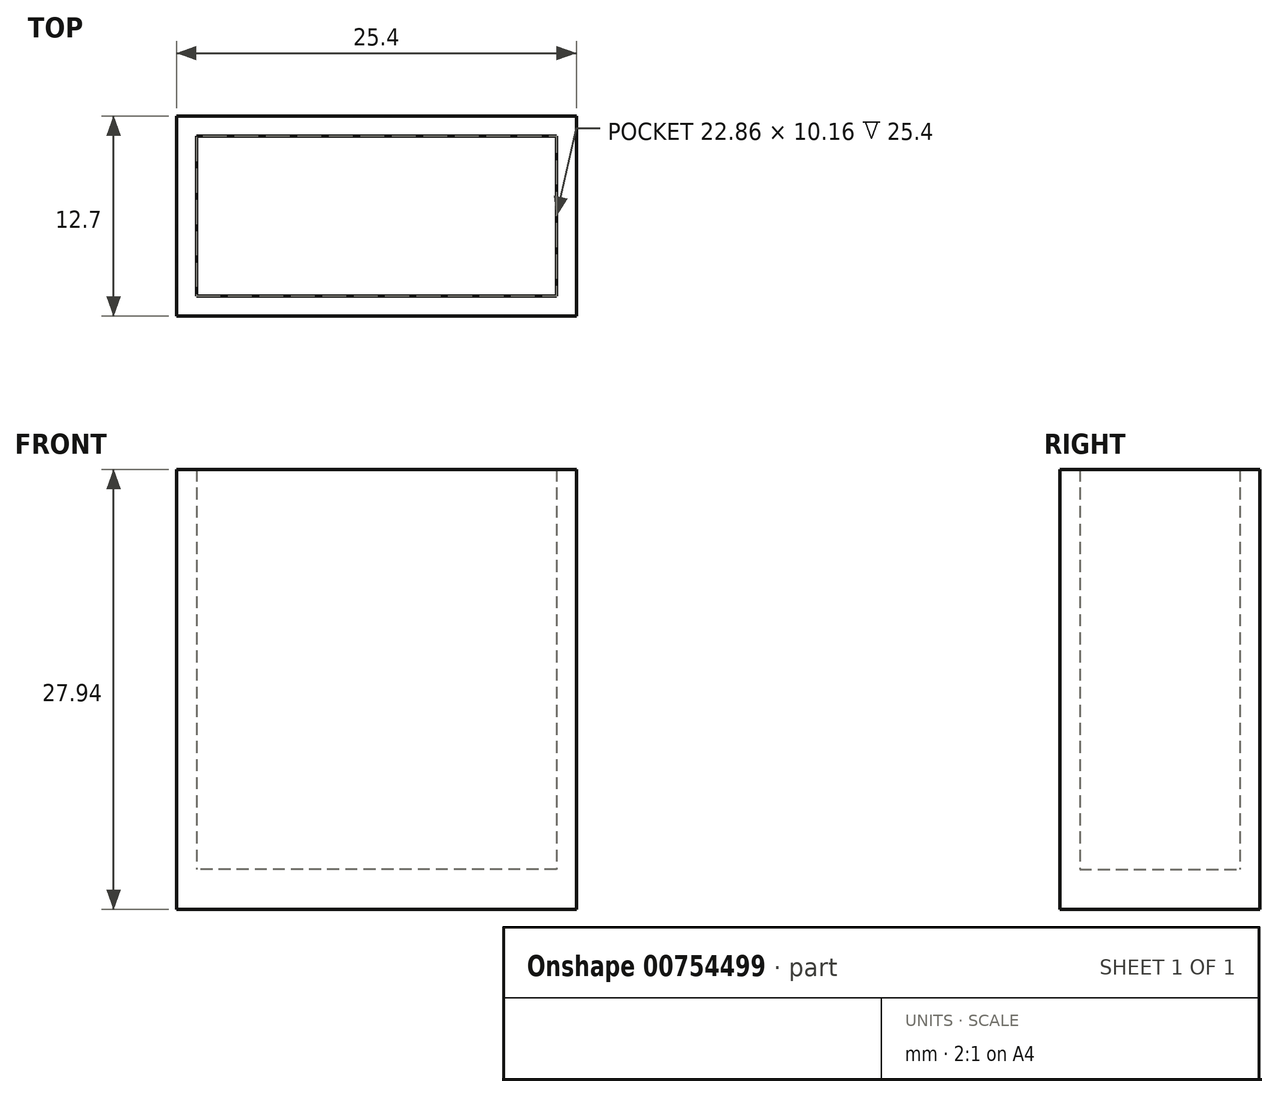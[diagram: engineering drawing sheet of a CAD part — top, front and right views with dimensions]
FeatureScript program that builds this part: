
annotation { "Feature Type Name" : "Feature", "Feature Type Description" : "" }
export const myFeature = defineFeature(function(context is Context, id is Id, definition is map)
    precondition{}
    {
        {
            var Q0;
            Q0=qCreatedBy(makeId("Top.planeOp"),FACE);
            var sketch = newSketch(context, id + "F0", { "sketchPlane" : qUnion([Q0])});
            skLineSegment(sketch, "E0.bottom", {"start": v(12.7, -6.35) * mm, "end": v(-12.7, -6.35) * mm});
            skLineSegment(sketch, "E0.top", {"start": v(12.7, 6.35) * mm, "end": v(-12.7, 6.35) * mm});
            skLineSegment(sketch, "E0.left", {"start": v(12.7, -6.35) * mm, "end": v(12.7, 6.35) * mm});
            skLineSegment(sketch, "E0.right", {"start": v(-12.7, -6.35) * mm, "end": v(-12.7, 6.35) * mm});
            skPoint(sketch, "E0.middle", {"position": v(0, 0) * mm});
            skLineSegment(sketch, "E1.0", {"start": v(-11.43, -5.08) * mm, "end": v(-11.43, 5.08) * mm});
            skLineSegment(sketch, "E1.1", {"start": v(11.43, -5.08) * mm, "end": v(-11.43, -5.08) * mm});
            skLineSegment(sketch, "E1.2", {"start": v(11.43, -5.08) * mm, "end": v(11.43, 5.08) * mm});
            skLineSegment(sketch, "E1.3", {"start": v(11.43, 5.08) * mm, "end": v(-11.43, 5.08) * mm});
            skSolve(sketch);
        }
        {
            var Q0;
            Q0=makeQuery(id+"F0.imprint","IMPRINT",FACE,{"disambiguationData":[TD([[makeQuery(id+"F0.imprint","IMPRINT",EDGE,{"derivedFrom":sQuery(id+"F0.wireOp",EDGE,"E0.bottom")}),-1.0]])]});
            extrude(context, id + "F1", {"entities" : qUnion([Q0]), "depth" : 25.4 * mm, "offsetDistance" : 25.4 * mm});
        }
        {
            var Q0;
            Q0=makeQuery(id+"F0.imprint","IMPRINT",FACE,{"disambiguationData":[TD([[makeQuery(id+"F0.imprint","IMPRINT",EDGE,{"derivedFrom":sQuery(id+"F0.wireOp",EDGE,"E1.0")}),-1.0]])]});
            var Q1;
            Q1=makeQuery(id+"F0.imprint","IMPRINT",FACE,{"disambiguationData":[TD([[makeQuery(id+"F0.imprint","IMPRINT",EDGE,{"derivedFrom":sQuery(id+"F0.wireOp",EDGE,"E0.bottom")}),-1.0]])]});
            extrude(context, id + "F2", {"entities" : qUnion([Q0, Q1]), "operationType" : NewBodyOperationType.ADD, "oppositeDirection" : true, "depth" : 2.54 * mm, "offsetDistance" : 25.4 * mm});
        }
    });
